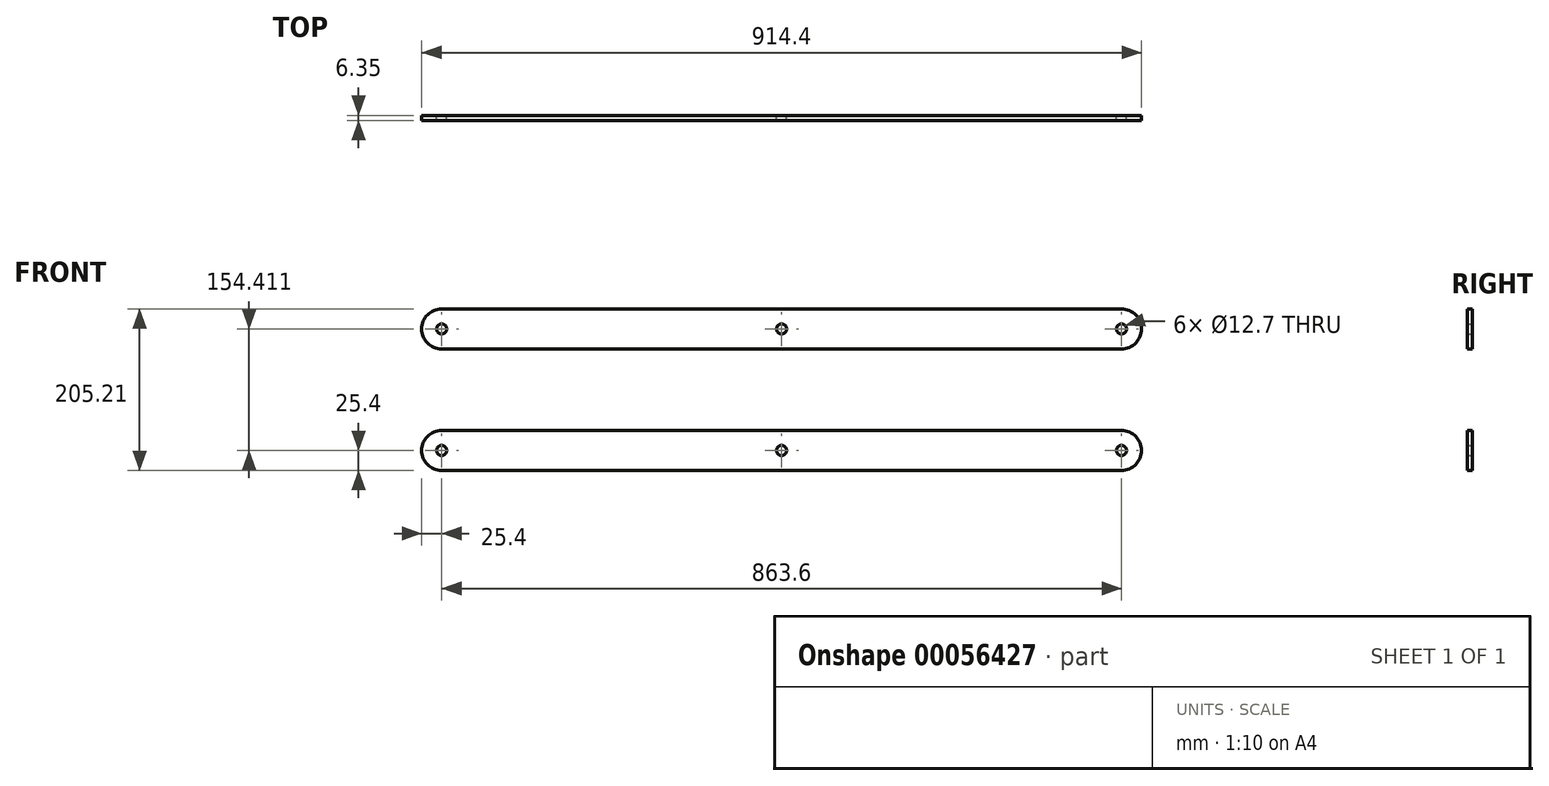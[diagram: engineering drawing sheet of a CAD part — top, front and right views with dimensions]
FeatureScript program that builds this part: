
annotation { "Feature Type Name" : "Feature", "Feature Type Description" : "" }
export const myFeature = defineFeature(function(context is Context, id is Id, definition is map)
    precondition{}
    {
        {
            var Q0;
            Q0=qCreatedBy(makeId("Front.planeOp"),FACE);
            var sketch = newSketch(context, id + "F0", { "sketchPlane" : qUnion([Q0])});
            skLineSegment(sketch, "E0.bottom", {"start": v(0, 0) * mm, "end": v(-863.6, 0) * mm});
            skLineSegment(sketch, "E0.top", {"start": v(0, 50.8) * mm, "end": v(-863.6, 50.8) * mm});
            skLineSegment(sketch, "E0.left", {"start": v(0, 0) * mm, "end": v(0, 50.8) * mm});
            skLineSegment(sketch, "E0.right", {"start": v(-863.6, 0) * mm, "end": v(-863.6, 50.8) * mm});
            skCircle(sketch, "E1", {"center": v(-863.6, 25.4) * mm, "radius": 25.4 * mm});
            skCircle(sketch, "E2", {"center": v(0, 25.4) * mm, "radius": 25.4 * mm});
            skCircle(sketch, "E3", {"center": v(-863.6, 25.4) * mm, "radius": 6.35 * mm});
            skCircle(sketch, "E4", {"center": v(0, 25.4) * mm, "radius": 6.35 * mm});
            skCircle(sketch, "E5", {"center": v(-431.8, 25.4) * mm, "radius": 25.4 * mm});
            skPoint(sketch, "E5.centerSnap0", {"position": v(-431.8, 0) * mm});
            skCircle(sketch, "E6", {"center": v(-431.8, 25.4) * mm, "radius": 6.35 * mm});
            skSolve(sketch);
        }
        {
            var Q0;
            {var subQ2=sQuery(id+"F0.wireOp",EDGE,"E0.bottom");var subQ4=sQuery(id+"F0.wireOp",EDGE,"E5");var subQ5=makeQuery(id+"F0.imprint","INTERSECT",VERTEX,{"derivedFrom":[subQ2,subQ4]});Q0=makeQuery(id+"F0.imprint","IMPRINT",FACE,{"disambiguationData":[TD([[makeQuery(id+"F0.imprint","IMPRINT",EDGE,{"disambiguationData":[TD([[subQ5,-1.0]])],"derivedFrom":subQ4}),-1.0]])]});}
            var Q1;
            {var subQ2=sQuery(id+"F0.wireOp",EDGE,"E0.bottom");var subQ4=sQuery(id+"F0.wireOp",EDGE,"E5");var subQ5=makeQuery(id+"F0.imprint","INTERSECT",VERTEX,{"derivedFrom":[subQ2,subQ4]});Q1=makeQuery(id+"F0.imprint","IMPRINT",FACE,{"disambiguationData":[TD([[makeQuery(id+"F0.imprint","IMPRINT",EDGE,{"disambiguationData":[TD([[subQ5,1.0]])],"derivedFrom":subQ4}),-1.0]])]});}
            var Q2;
            {var subQ1=sQuery(id+"F0.wireOp",EDGE,"E0.left");var subQ3=sQuery(id+"F0.wireOp",EDGE,"E4");var subQ4=makeQuery(id+"F0.imprint","INTERSECT",VERTEX,{"disambiguationData":[OD(0.0)],"derivedFrom":[subQ1,subQ3]});Q2=makeQuery(id+"F0.imprint","IMPRINT",FACE,{"disambiguationData":[TD([[makeQuery(id+"F0.imprint","IMPRINT",EDGE,{"disambiguationData":[TD([[subQ4,-1.0]])],"derivedFrom":subQ3}),-1.0]])]});}
            var Q3;
            {var subQ1=sQuery(id+"F0.wireOp",EDGE,"E0.right");var subQ3=sQuery(id+"F0.wireOp",EDGE,"E3");var subQ4=makeQuery(id+"F0.imprint","INTERSECT",VERTEX,{"disambiguationData":[OD(0.0)],"derivedFrom":[subQ1,subQ3]});Q3=makeQuery(id+"F0.imprint","IMPRINT",FACE,{"disambiguationData":[TD([[makeQuery(id+"F0.imprint","IMPRINT",EDGE,{"disambiguationData":[TD([[subQ4,1.0]])],"derivedFrom":subQ3}),-1.0]])]});}
            var Q4;
            {var subQ1=sQuery(id+"F0.wireOp",EDGE,"E0.left");var subQ3=sQuery(id+"F0.wireOp",EDGE,"E4");var subQ4=makeQuery(id+"F0.imprint","INTERSECT",VERTEX,{"disambiguationData":[OD(0.0)],"derivedFrom":[subQ1,subQ3]});Q4=makeQuery(id+"F0.imprint","IMPRINT",FACE,{"disambiguationData":[TD([[makeQuery(id+"F0.imprint","IMPRINT",EDGE,{"disambiguationData":[TD([[subQ4,1.0]])],"derivedFrom":subQ3}),-1.0]])]});}
            var Q5;
            Q5=makeQuery(id+"F0.imprint","IMPRINT",FACE,{"disambiguationData":[TD([[makeQuery(id+"F0.imprint","IMPRINT",EDGE,{"derivedFrom":sQuery(id+"F0.wireOp",EDGE,"E6")}),-1.0]])]});
            var Q6;
            {var subQ1=sQuery(id+"F0.wireOp",EDGE,"E0.right");var subQ3=sQuery(id+"F0.wireOp",EDGE,"E3");var subQ4=makeQuery(id+"F0.imprint","INTERSECT",VERTEX,{"disambiguationData":[OD(0.0)],"derivedFrom":[subQ1,subQ3]});Q6=makeQuery(id+"F0.imprint","IMPRINT",FACE,{"disambiguationData":[TD([[makeQuery(id+"F0.imprint","IMPRINT",EDGE,{"disambiguationData":[TD([[subQ4,-1.0]])],"derivedFrom":subQ3}),-1.0]])]});}
            extrude(context, id + "F1", {"entities" : qUnion([Q0, Q1, Q2, Q3, Q4, Q5, Q6]), "depth" : 6.35 * mm});
        }
        {
            var Q0;
            Q0=makeQuery(id+"F1.opExtrude","SWEPT_BODY",BODY,{"disambiguationData":[OSD([sQuery(id+"F0.wireOp",EDGE,"E0.bottom"),sQuery(id+"F0.wireOp",EDGE,"E0.top"),sQuery(id+"F0.wireOp",EDGE,"E1"),sQuery(id+"F0.wireOp",EDGE,"E2"),sQuery(id+"F0.wireOp",EDGE,"E3"),sQuery(id+"F0.wireOp",EDGE,"E4"),sQuery(id+"F0.wireOp",EDGE,"E6")])]});
            transform(context, id + "F2", {"entities" : qUnion([Q0]), "transformType" : TransformType.TRANSLATION_3D, "dx" : 0 * mm, "dy" : 0 * mm, "dz" : 154.4 * mm, "makeCopy" : true});
        }
    });
